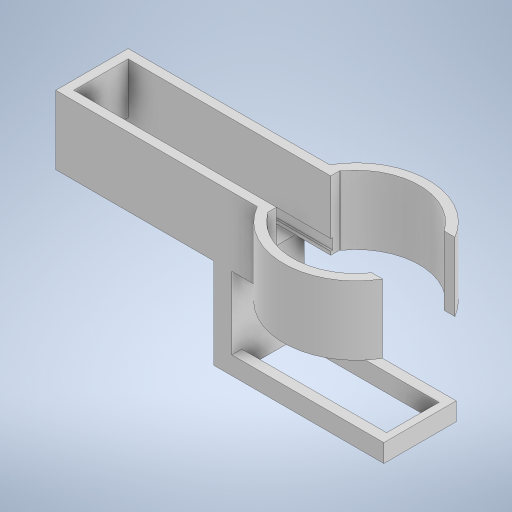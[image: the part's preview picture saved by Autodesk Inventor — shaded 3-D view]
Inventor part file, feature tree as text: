
AUTODESK INVENTOR PART (.ipt)
format: ipt  version: 2023 (Build 270158000, 158)  size: 599,552 bytes
history: native  units: mm
features: sketch x13, extrude x10, projected_geometry x2
ambient origin geometry x8: Origin, YZ Plane, XZ Plane, XY Plane, X Axis, Y Axis, Z Axis, Center Point
bodies: Solid1 (feature_tree)
feature tree (25):
  extrude  "Extrusion1"  Depth=20.0mm
  extrude  "Extrusion2"  Depth=2.5mm
  extrude  "Extrusion3"  Depth=2.5mm
  sketch  "Sketch4"  dims[d7=14.0mm d8=0.0mm d9=15.0mm]
  extrude  "Extrusion4"  Depth=15.0mm
  extrude  "Extrusion5"  Depth=20.0mm
  sketch  "Sketch8"  dims[d15=14.0mm d16=0.0mm d17=15.0mm]
  extrude  "Extrusion6"  Depth=40.0mm
  extrude  "Extrusion7"  Depth=15.0mm
  extrude  "Extrusion8"  Depth=2.0mm
  extrude  "Extrusion9"  Depth=2.5mm TaperAngle=0.0deg
  extrude  "Extrusion10"  Depth=25.0mm
  sketch  "Sketch14"  dims[d29=3.0mm d30=0.0mm d34=10.0mm d35=0.0mm d36=35.0mm d37=14.5mm d38=5.0mm d39=2.75mm d40=0.0mm d41=0.0mm d42=2.0mm d43=1.0mm d44=1.0mm d45=2.0mm d46=1.0mm d47=1.0mm d49=2.5mm d50=5.0mm d51=0.0mm d52=7.0mm d53=0.0mm d54=5.0mm d55=0.0mm d24=0.872665mm]
  sketch  "Sketch1"  dims[d0=60.0mm d1=20.0mm]
  sketch  "Sketch2"  dims[d2=5.0mm d3=0.0mm d4=2.5mm]
  sketch  "Sketch3"  dims[d5=2.5mm d6=2.5mm]
  projected_geometry  "Projected Loop1"
  projected_geometry  "Projected Loop2"
  sketch  "Sketch5"  dims[d10=26.0mm d11=20.0mm]
  sketch  "Sketch7"  dims[d13=35.0mm d14=40.0mm]
  sketch  "Sketch9"  dims[d18=5.0mm d19=0.0mm d20=2.0mm]
  sketch  "Sketch10"  dims[d21=2.5mm d22=1.5mm d23=0.0mm]
  sketch  "Sketch11"  dims[d25=7.0mm d26=25.0mm]
  sketch  "Sketch12"  dims[d27=35.0mm]
  sketch  "Sketch13"  dims[d28=5.0mm]
